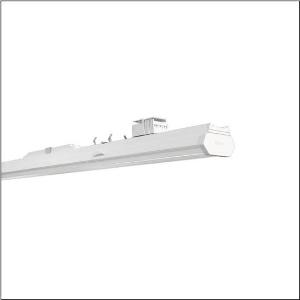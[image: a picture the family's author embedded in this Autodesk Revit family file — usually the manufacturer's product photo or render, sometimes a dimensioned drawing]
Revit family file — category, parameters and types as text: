
# Revit family: licross_11_protected_mo_51tp12mn695g
name_source: partatom
category: Lighting Fixtures
units: mm (PartAtom-declared; Revit-internal decimal feet)

## family parameters
Cut with Voids When Loaded = No
Host = Face
Light Source = No
Part Type = Normal
Room Calculation Point = No
Round Connector Dimension = Use Diameter
Shared = No

## types (1)
- --- (1 x LED, 9780 lm, 55.3 W, 6500K)
    Apparent Load = 55 VA
    CIE Flux Codes = 73 92 98 99 100
    Color Rendering = 80
    Color Temperature = 6500K
    Default Elevation = 1800 mm
    Description = Licross 11 Protected MO, luminaire insert, of sheet steel, galvanised, coil coated, white, length: 1.500mm, width: 90mm, height: 101mm, LED rated luminous flux: 9.780lm, light colour: 865, SDCM (Standard Deviation of Colour Matching)MacAdam ≤ 2 SDCM (initial), control gear: ON/OFF Multilumen, with plug, 3-pole, with phase selection, mains connection: 220..240V, AC, 50/60Hz, rated input power: 55W, internal wiring halogen-free, primary light control with lens, of plastic, primary optical cover: cover, of PMMA, light emission: direct distribution, primary light characteristic: symmetric, protection rating (complete): IP64, insulation class (complete): insulation class I (protective earthing), certification: CE, ENEC, VDE, UKCA, protection symbol: D if used in an environment with conductive dust loads with corresponding accessories, impact resistance: IK06, permissible ambient temperature for indoor applications: -35..+40°C, corresponds to IFS (International Featured Standards) requirements for safety and quality in the food industry, reducing of maximum allowable ambient temperature of 5°C with ceiling mounting, LABS conformity tested according to VDMA 24364:2018-05, The light source and the operating device comply with the requirements of the Ecodesign Regulation (EU) 2019/2020 and are replaceable in accordance with this regulation, packaging unit: 1 piece
    Height = 92 mm
    Lamp = 1 x LED
    Lamp Light Flux = 9780 lm
    Lamp Power = 55.3 W
    Lamp count = 1
    Length = 1500 mm
    Luminous efficacy = 177 lm/W
    Manufacturer = Siteco
    ModVariant = No
    Model = 51TP12MN695G
    Mounting Place = Ceiling
    Mounting Type = Pendant
    Number of Poles = 1
    OnlyDefault = Yes
    Power Factor = 1
    Product Name = Licross 11 Protected MO
    Product group = luminaire insert | ceiling pendant
    ProductGroupID = 901
    Protection Class = Protection class I
    Protection Degree = IP 64
    RLX_Detail_Level = 1
    RLX_Emergency_Light_Flux = 0 lm
    RLX_Emergency_Type = 0
    RLX_Emergency_Type_DB = No
    RlxData = <blob elided: 22373 chars, md5=caa1c281>
    Socket = socket
    Standby Power = 0 W
    System Light Flux = 9780 lm
    System Power = 55 W
    Type Comments = factory setting: luminous flux: 100 % | (A | C | E) | 126 mA
    Type Image = l_1256148.jpg
    URL = http://relux.com
    VarID = @adj_039657
    Voltage = 0 V
    Weight = 0.00 kg
    Width = 88 mm

## geometry (parser evidence)
native form markers: Blend x4, Sweep x12
no freeform markers — native parametric forms only
